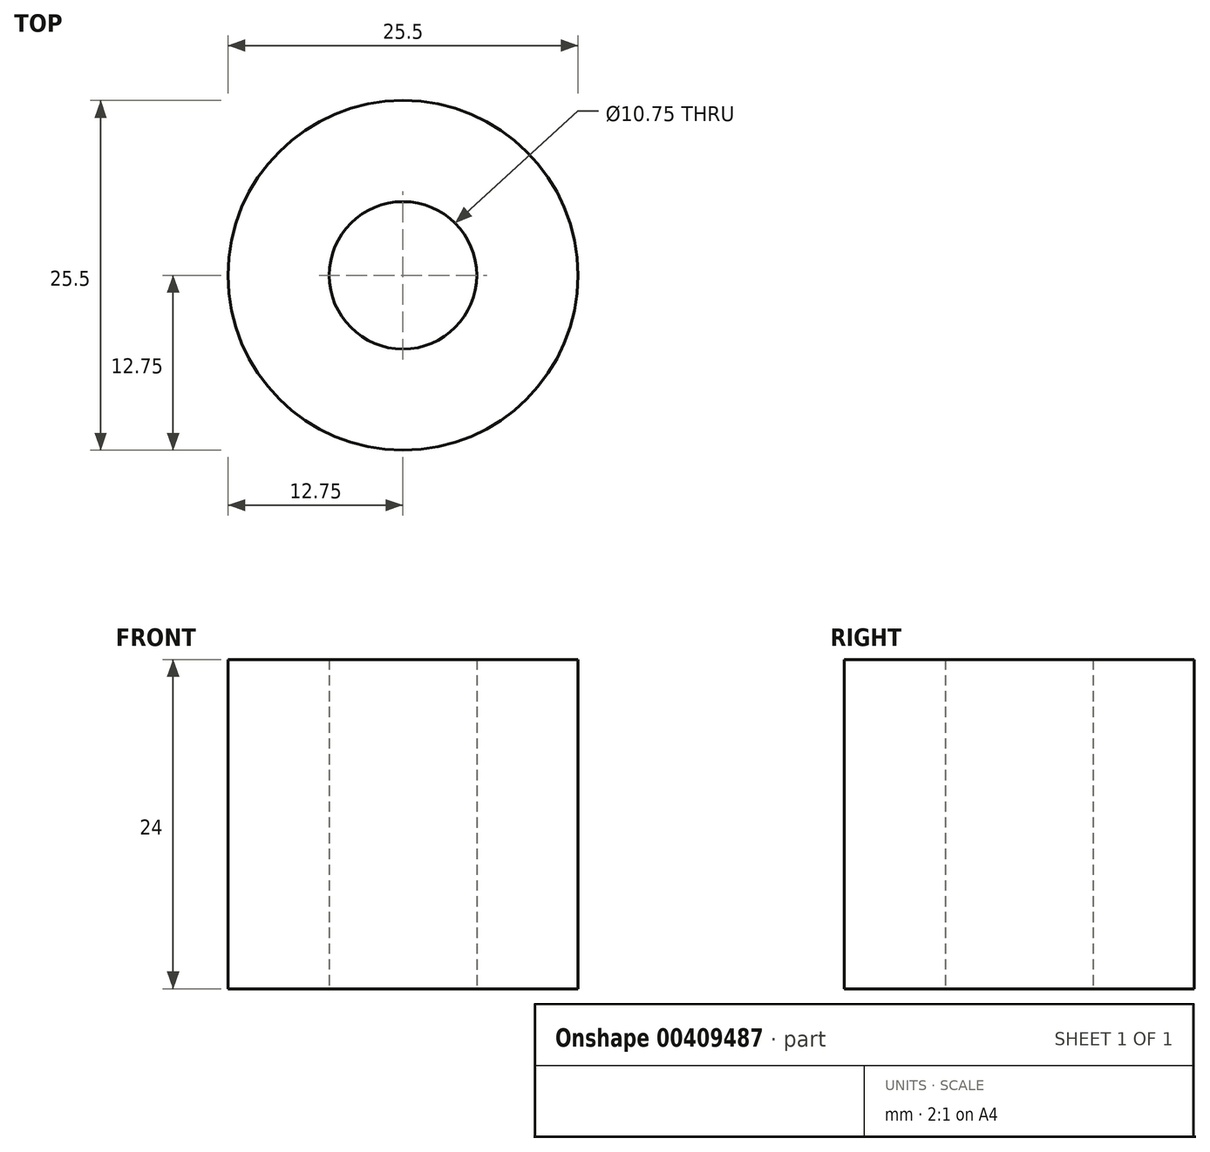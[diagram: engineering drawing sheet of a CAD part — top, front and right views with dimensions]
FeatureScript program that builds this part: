
annotation { "Feature Type Name" : "Feature", "Feature Type Description" : "" }
export const myFeature = defineFeature(function(context is Context, id is Id, definition is map)
    precondition{}
    {
        {
            var Q0;
            Q0=qCreatedBy(makeId("Top.planeOp"),FACE);
            var sketch = newSketch(context, id + "F0", { "sketchPlane" : qUnion([Q0])});
            skCircle(sketch, "E0", {"center": v(0, 0) * mm, "radius": 5.38 * mm});
            skCircle(sketch, "E1", {"center": v(0, 0) * mm, "radius": 12.75 * mm});
            skSolve(sketch);
        }
        {
            var Q0;
            Q0=makeQuery(id+"F0.imprint","IMPRINT",FACE,{"disambiguationData":[TD([[makeQuery(id+"F0.imprint","IMPRINT",EDGE,{"derivedFrom":sQuery(id+"F0.wireOp",EDGE,"E0")}),-1.0]])]});
            extrude(context, id + "F1", {"entities" : qUnion([Q0]), "depth" : 24 * mm});
        }
    });
